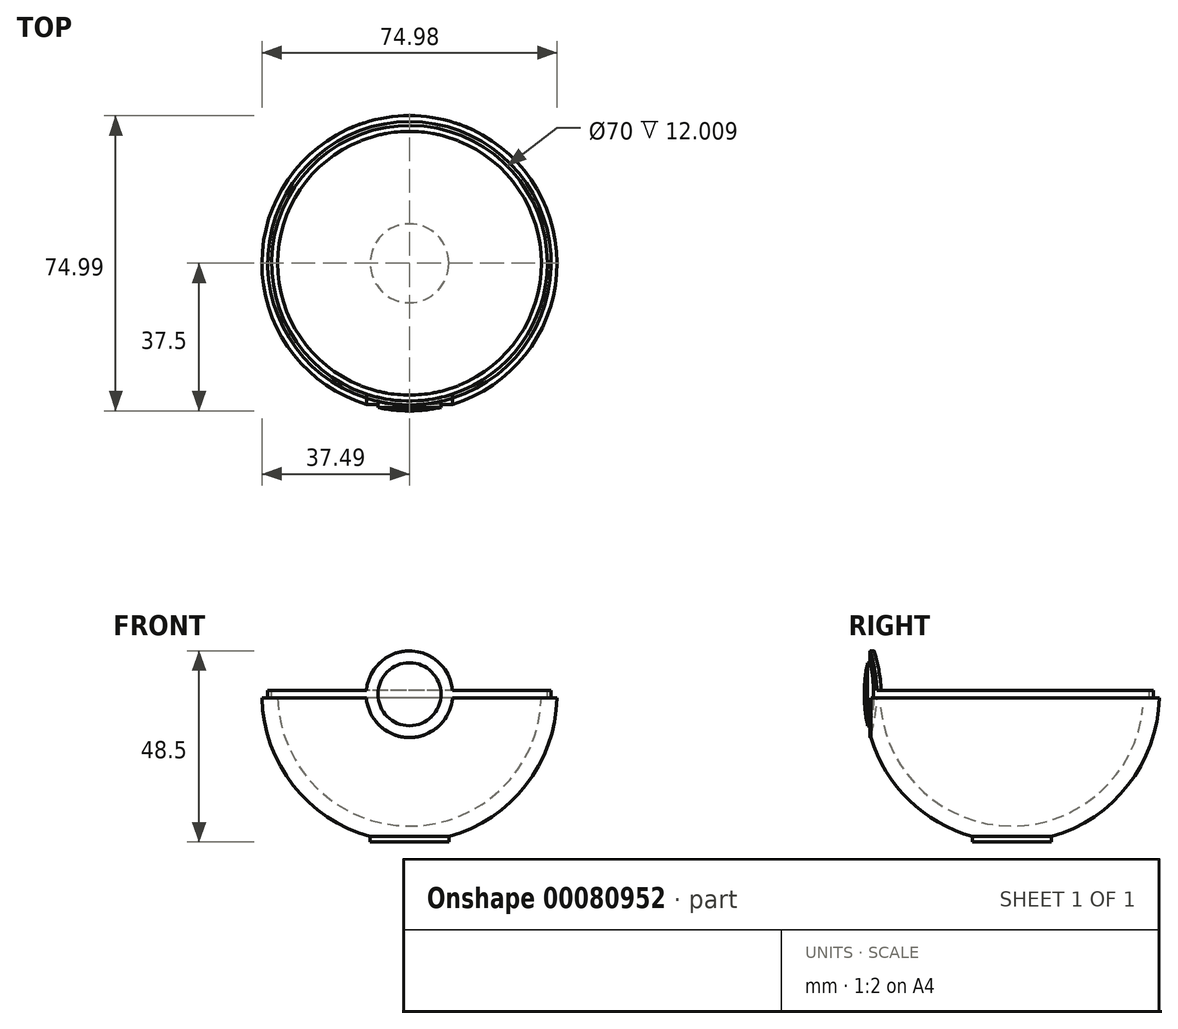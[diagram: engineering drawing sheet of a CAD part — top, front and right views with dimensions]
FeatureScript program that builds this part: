
annotation { "Feature Type Name" : "Feature", "Feature Type Description" : "" }
export const myFeature = defineFeature(function(context is Context, id is Id, definition is map)
    precondition{}
    {
        {
            var Q0;
            Q0=qCreatedBy(makeId("Top.planeOp"),FACE);
            var sketch = newSketch(context, id + "F0", { "sketchPlane" : qUnion([Q0])});
            skCircle(sketch, "E0", {"center": v(0, 0) * mm, "radius": 37.5 * mm});
            skCircle(sketch, "E1.0", {"center": v(0, 0) * mm, "radius": 33.5 * mm});
            skLineSegment(sketch, "E2", {"start": v(0, 37.5) * mm, "end": v(0, -37.5) * mm, "construction": true});
            skPoint(sketch, "E3", {"position": v(0, 33.5) * mm});
            skPoint(sketch, "E4", {"position": v(0, -33.5) * mm});
            skLineSegment(sketch, "E5", {"start": v(0, 33.5) * mm, "end": v(0, 37.5) * mm});
            skLineSegment(sketch, "E6", {"start": v(0, -33.5) * mm, "end": v(0, -37.5) * mm});
            skCircle(sketch, "E7", {"center": v(0, 0) * mm, "radius": 10 * mm});
            skPoint(sketch, "E8", {"position": v(0, -37.5) * mm});
            skPoint(sketch, "E9", {"position": v(0, 37.5) * mm});
            skCircle(sketch, "E10", {"center": v(0, 0) * mm, "radius": 36 * mm});
            skCircle(sketch, "E11", {"center": v(0, 0) * mm, "radius": 35 * mm});
            skPoint(sketch, "E12", {"position": v(0, -35) * mm});
            skPoint(sketch, "E13", {"position": v(0, -36) * mm});
            skSolve(sketch);
        }
        {
            var Q0;
            {var subQ0=sQuery(id+"F0.wireOp",EDGE,"E5");Q0=makeQuery(id+"F0.imprint","IMPRINT",FACE,{"disambiguationData":[TD([[makeQuery(id+"F0.imprint","IMPRINT",EDGE,{"derivedFrom":subQ0}),1.0]])]});}
            var Q1;
            Q1=sQuery(id+"F0.wireOp",EDGE,"E2");
            revolve(context, id + "F1", {"entities" : qUnion([Q0]), "axis" : qUnion([Q1]), "revolveType" : RevolveType.ONE_DIRECTION, "angle" : 180 * degree});
        }
        {
            var Q0;
            Q0=qCreatedBy(makeId("Right.planeOp"),FACE);
            var sketch = newSketch(context, id + "F2", { "sketchPlane" : qUnion([Q0])});
            skArc(sketch, "E14", {"start": v(-37.5, 0) * mm, "mid": v(0, -37.5) * mm, "end": v(37.5, 0) * mm});
            skPoint(sketch, "E15", {"position": v(0, -37.5) * mm});
            skSolve(sketch);
        }
        {
            var Q0;
            Q0=sQuery(id+"F2.wireOp",VERTEX,"E15");
            var Q1;
            {var subQ0=sQuery(id+"F0.wireOp",EDGE,"E5");var subQ1=sQuery(id+"F0.wireOp",EDGE,"E0");var subQ2=makeQuery(id+"F0.imprint","INTERSECT",VERTEX,{"derivedFrom":[subQ1,subQ0]});Q1=makeQuery(id+"F0.imprint","IMPRINT",FACE,{"disambiguationData":[TD([[makeQuery(id+"F0.imprint","IMPRINT",EDGE,{"disambiguationData":[TD([[subQ2,1.0]])],"derivedFrom":subQ1}),1.0]])]});}
            cPlane(context, id + "F3", {"entities" : qUnion([Q0, Q1]), "cplaneType" : CPlaneType.PLANE_POINT, "offset" : 150 * mm, "width" : 150 * mm, "height" : 150 * mm});
        }
        {
            var Q0;
            Q0=qCreatedBy(id+"F3.planeOp",FACE);
            var sketch = newSketch(context, id + "F4", { "sketchPlane" : qUnion([Q0])});
            skCircle(sketch, "E16.0", {"center": v(0, 0) * mm, "radius": 10 * mm});
            skSolve(sketch);
        }
        {
            var Q0;
            Q0=makeQuery(id+"F4.imprint","IMPRINT",FACE,{"disambiguationData":[TD([[makeQuery(id+"F4.imprint","IMPRINT",EDGE,{"derivedFrom":sQuery(id+"F4.wireOp",EDGE,"E16.0")}),1.0]])]});
            var Q1;
            Q1=makeQuery(id+"F1.opRevolve","SWEPT_FACE",FACE,{"disambiguationData":[OSD([sQuery(id+"F0.wireOp",EDGE,"E1.0")])]});
            extrude(context, id + "F5", {"entities" : qUnion([Q0]), "operationType" : NewBodyOperationType.ADD, "endBound" : BoundingType.UP_TO_SURFACE, "endBoundEntityFace" : qUnion([Q1]), "depth" : 25 * mm});
        }
        {
            var Q0;
            Q0=qCreatedBy(makeId("Front.planeOp"),FACE);
            var Q1;
            Q1=sQuery(id+"F0.wireOp",VERTEX,"E8");
            cPlane(context, id + "F6", {"entities" : qUnion([Q0, Q1]), "cplaneType" : CPlaneType.PLANE_POINT, "offset" : 150 * mm, "width" : 150 * mm, "height" : 150 * mm});
        }
        {
            var Q0;
            Q0=qCreatedBy(id+"F6.planeOp",FACE);
            var sketch = newSketch(context, id + "F7", { "sketchPlane" : qUnion([Q0])});
            skCircle(sketch, "E17", {"center": v(0, 0) * mm, "radius": 8 * mm});
            skCircle(sketch, "E18.0", {"center": v(0, 0) * mm, "radius": 11 * mm});
            skSolve(sketch);
        }
        {
            var Q0;
            {var subQ0=sQuery(id+"F0.wireOp",EDGE,"E5");var subQ1=sQuery(id+"F0.wireOp",EDGE,"E0");var subQ2=makeQuery(id+"F0.imprint","INTERSECT",VERTEX,{"derivedFrom":[subQ1,subQ0]});Q0=makeQuery(id+"F0.imprint","IMPRINT",FACE,{"disambiguationData":[TD([[makeQuery(id+"F0.imprint","IMPRINT",EDGE,{"disambiguationData":[TD([[subQ2,1.0]])],"derivedFrom":subQ1}),1.0]])]});}
            var Q1;
            {var subQ0=sQuery(id+"F0.wireOp",EDGE,"E5");var subQ1=sQuery(id+"F0.wireOp",EDGE,"E0");var subQ2=makeQuery(id+"F0.imprint","INTERSECT",VERTEX,{"derivedFrom":[subQ1,subQ0]});Q1=makeQuery(id+"F0.imprint","IMPRINT",FACE,{"disambiguationData":[TD([[makeQuery(id+"F0.imprint","IMPRINT",EDGE,{"disambiguationData":[TD([[subQ2,-1.0]])],"derivedFrom":subQ1}),1.0]])]});}
            var Q2;
            {var subQ0=sQuery(id+"F0.wireOp",EDGE,"E5");var subQ1=sQuery(id+"F0.wireOp",EDGE,"E1.0");var subQ2=makeQuery(id+"F0.imprint","INTERSECT",VERTEX,{"derivedFrom":[subQ1,subQ0]});Q2=makeQuery(id+"F0.imprint","IMPRINT",FACE,{"disambiguationData":[TD([[makeQuery(id+"F0.imprint","IMPRINT",EDGE,{"disambiguationData":[TD([[subQ2,1.0]])],"derivedFrom":subQ1}),-1.0]])]});}
            var Q3;
            {var subQ0=sQuery(id+"F0.wireOp",EDGE,"E5");var subQ1=sQuery(id+"F0.wireOp",EDGE,"E1.0");var subQ2=makeQuery(id+"F0.imprint","INTERSECT",VERTEX,{"derivedFrom":[subQ1,subQ0]});Q3=makeQuery(id+"F0.imprint","IMPRINT",FACE,{"disambiguationData":[TD([[makeQuery(id+"F0.imprint","IMPRINT",EDGE,{"disambiguationData":[TD([[subQ2,-1.0]])],"derivedFrom":subQ1}),-1.0]])]});}
            var Q4;
            Q4=makeQuery(id+"F0.imprint","IMPRINT",FACE,{"disambiguationData":[TD([[makeQuery(id+"F0.imprint","IMPRINT",EDGE,{"derivedFrom":sQuery(id+"F0.wireOp",EDGE,"E7")}),-1.0]])]});
            extrude(context, id + "F8", {"entities" : qUnion([Q0, Q1, Q2, Q3, Q4]), "operationType" : NewBodyOperationType.REMOVE, "oppositeDirection" : true, "depth" : 1 * mm});
        }
        {
            var Q0;
            Q0=makeQuery(id+"F7.imprint","IMPRINT",FACE,{"disambiguationData":[TD([[makeQuery(id+"F7.imprint","IMPRINT",EDGE,{"derivedFrom":sQuery(id+"F7.wireOp",EDGE,"E17")}),-1.0]])]});
            var Q1;
            Q1=makeQuery(id+"F8.boolean.opBoolean","COPY",FACE,{"derivedFrom":makeQuery(id+"F8.opExtrude","SWEPT_FACE",FACE,{"disambiguationData":[OSD([sQuery(id+"F0.wireOp",EDGE,"E10")])]})});
            extrude(context, id + "F9", {"entities" : qUnion([Q0]), "operationType" : NewBodyOperationType.REMOVE, "endBound" : BoundingType.UP_TO_SURFACE, "oppositeDirection" : true, "endBoundEntityFace" : qUnion([Q1]), "depth" : 25 * mm});
        }
        {
            var Q0;
            Q0=makeQuery(id+"F1.opRevolve","CAP_FACE",FACE,{"disambiguationData":[OSD([sQuery(id+"F0.wireOp",EDGE,"E0"),sQuery(id+"F0.wireOp",EDGE,"E1.0"),sQuery(id+"F0.wireOp",EDGE,"E5"),sQuery(id+"F0.wireOp",EDGE,"E6")])],"isStart":false});
            extrude(context, id + "F10", {"entities" : qUnion([Q0]), "operationType" : NewBodyOperationType.ADD, "depth" : 1 * mm});
        }
        {
            var Q0;
            Q0=makeQuery(id+"F7.imprint","IMPRINT",FACE,{"disambiguationData":[TD([[makeQuery(id+"F7.imprint","IMPRINT",EDGE,{"derivedFrom":sQuery(id+"F7.wireOp",EDGE,"E17")}),1.0]])]});
            var Q1;
            Q1=makeQuery(id+"F8.boolean.opBoolean","COPY",FACE,{"derivedFrom":makeQuery(id+"F8.opExtrude","SWEPT_FACE",FACE,{"disambiguationData":[OSD([sQuery(id+"F0.wireOp",EDGE,"E11")])]})});
            var Q2;
            {var subQ1=sQuery(id+"F0.wireOp",EDGE,"E0");Q2=makeQuery(id+"F9.boolean.opBoolean","SPLIT",FACE,{"disambiguationData":[TD([makeQuery(id+"F5.opExtrude","SWEPT_FACE",FACE,{"disambiguationData":[OSD([sQuery(id+"F4.wireOp",EDGE,"E16.0")])]})])],"derivedFrom":makeQuery(id+"F1.opRevolve","SWEPT_FACE",FACE,{"disambiguationData":[OSD([subQ1])]})});}
            extrude(context, id + "F11", {"entities" : qUnion([Q0]), "operationType" : NewBodyOperationType.ADD, "endBound" : BoundingType.UP_TO_SURFACE, "oppositeDirection" : true, "endBoundEntityFace" : qUnion([Q1]), "depth" : 25 * mm, "hasSecondDirection" : true, "secondDirectionBound" : SecondDirectionBoundingType.UP_TO_SURFACE, "secondDirectionOppositeDirection" : true, "secondDirectionBoundEntityFace" : qUnion([Q2]), "secondDirectionDepth" : 25 * mm});
        }
        {
            var Q0;
            Q0=sQuery(id+"F0.wireOp",VERTEX,"E12");
            var Q1;
            Q1=qCreatedBy(makeId("Front.planeOp"),FACE);
            cPlane(context, id + "F12", {"entities" : qUnion([Q0, Q1]), "cplaneType" : CPlaneType.PLANE_POINT, "offset" : 150 * mm, "width" : 150 * mm, "height" : 150 * mm});
        }
        {
            var Q0;
            Q0=qCreatedBy(id+"F12.planeOp",FACE);
            var sketch = newSketch(context, id + "F13", { "sketchPlane" : qUnion([Q0])});
            skCircle(sketch, "E19.0", {"center": v(0, 0) * mm, "radius": 11 * mm});
            skSolve(sketch);
        }
        {
            var Q0;
            Q0=makeQuery(id+"F13.imprint","IMPRINT",FACE,{"disambiguationData":[TD([[makeQuery(id+"F13.imprint","IMPRINT",EDGE,{"derivedFrom":sQuery(id+"F13.wireOp",EDGE,"E19.0")}),1.0]])]});
            var Q1;
            {var subQ0=sQuery(id+"F0.wireOp",EDGE,"E10");Q1=makeQuery(id+"F10.boolean.opBoolean","MERGE",FACE,{"derivedFrom":[makeQuery(id+"F9.boolean.opBoolean","MERGE",FACE,{"derivedFrom":[makeQuery(id+"F8.boolean.opBoolean","COPY",FACE,{"derivedFrom":makeQuery(id+"F8.opExtrude","SWEPT_FACE",FACE,{"disambiguationData":[OSD([subQ0])]})}),makeQuery(id+"F9.opExtrude","CAP_FACE",FACE,{"disambiguationData":[OSD([subQ0])],"isStart":false})]}),makeQuery(id+"F10.opExtrude","SWEPT_FACE",FACE,{"disambiguationData":[OSD([subQ0])]})]});}
            var Q2;
            {var subQ0=sQuery(id+"F0.wireOp",EDGE,"E11");Q2=makeQuery(id+"F11.boolean.opBoolean","MERGE",FACE,{"derivedFrom":[makeQuery(id+"F10.boolean.opBoolean","MERGE",FACE,{"derivedFrom":[makeQuery(id+"F8.boolean.opBoolean","COPY",FACE,{"derivedFrom":makeQuery(id+"F8.opExtrude","SWEPT_FACE",FACE,{"disambiguationData":[OSD([subQ0])]})}),makeQuery(id+"F10.opExtrude","SWEPT_FACE",FACE,{"disambiguationData":[OSD([subQ0])]})]}),makeQuery(id+"F11.opExtrude","CAP_FACE",FACE,{"disambiguationData":[OSD([subQ0])],"isStart":false})]});}
            extrude(context, id + "F14", {"entities" : qUnion([Q0]), "operationType" : NewBodyOperationType.ADD, "endBound" : BoundingType.UP_TO_SURFACE, "endBoundEntityFace" : qUnion([Q1]), "depth" : 25 * mm, "hasSecondDirection" : true, "secondDirectionBound" : SecondDirectionBoundingType.UP_TO_SURFACE, "secondDirectionOppositeDirection" : true, "secondDirectionBoundEntityFace" : qUnion([Q2]), "secondDirectionDepth" : 25 * mm});
        }
    });
